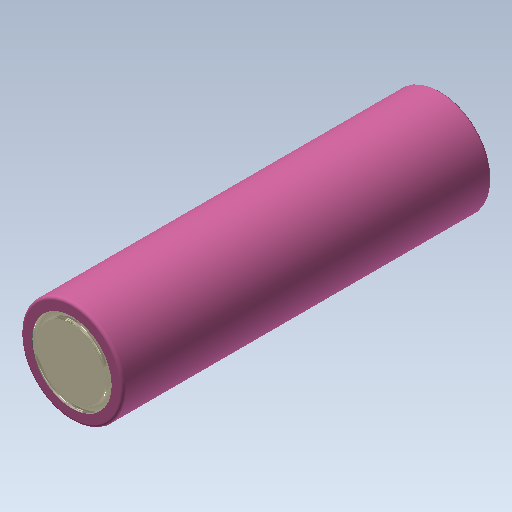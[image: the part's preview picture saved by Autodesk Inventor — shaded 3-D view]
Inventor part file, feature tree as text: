
AUTODESK INVENTOR PART (.ipt)
format: ipt  version: 2020 (Build 240168000, 168)  size: 890,368 bytes
history: native  units: mm
features: sketch x5, extrude x4, fillet x3, plane x1, emboss x1
ambient origin geometry x8: Origin, YZ Plane, XZ Plane, XY Plane, X Axis, Y Axis, Z Axis, Center Point
bodies: Solid1 (feature_tree)
feature tree (14):
  extrude  "Extrusion1"  Depth=64.7mm TaperAngle=0.0deg
  extrude  "Extrusion2"  Depth=0.1mm TaperAngle=0.0deg
  extrude  "Extrusion3"  Depth=0.1mm TaperAngle=0.0deg
  fillet  "Fillet1"  Radius=0.5mm
  extrude  "Extrusion4"  Depth=12.0mm
  fillet  "Fillet2"  Radius=0.6mm
  fillet  "Fillet3"  Radius=0.5mm
  plane  "Work Plane1"
  emboss  "Emboss1"
  sketch  "Sketch1"  dims[d0=18.0mm d1=64.7mm d2=0.0mm]
  sketch  "Sketch2"  dims[d3=12.0mm d4=0.1mm d5=0.0mm]
  sketch  "Sketch3"  dims[d6=14.0mm d7=0.1mm d8=0.0mm d9=0.5mm]
  sketch  "Sketch4"  dims[d10=14.0mm d11=12.0mm d12=0.6mm d13=0.0mm d14=0.5mm]
  sketch  "Sketch5"  dims[d15=0.1mm d16=-9.0mm d17=55.0mm d18=0.01mm d19=0.0mm]
